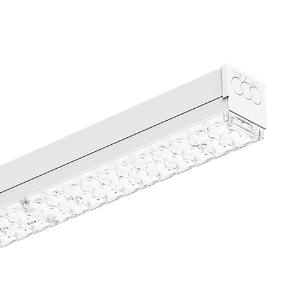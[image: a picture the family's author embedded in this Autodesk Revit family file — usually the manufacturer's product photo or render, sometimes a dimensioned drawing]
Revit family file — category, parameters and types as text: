
# Revit family: 3f_filippi_-_3f_zeta_l_ugr_3f_filippi_-_10841_-_3f_zeta_l_ugr_40-940_led_dali_l1489
name_source: partatom
category: Lighting Fixtures
units: mm (PartAtom-declared; Revit-internal decimal feet)

## family parameters
Cut with Voids When Loaded = No
Host = Face
Light Source = No
Part Type = Normal
Room Calculation Point = No
Round Connector Dimension = Use Diameter
Shared = No

## types (1)
- 3F Filippi - 3F Zeta L UGR (1 x LED, 5310 lm, 40 W, 4000 K)
    Apparent Load = 40 VA
    Approval mark = ENEC
    CIE Flux Codes = 83 96 99 97 100
    Color Rendering = 90
    Color Temperature = 4000 K
    Control Gear = Electronic transformer
    Default Elevation = 1800 mm
    Description = ILLUMINOTECHNICAL
Luminous efficiency 100% (DLOR 97%, ULOR 3%).
Initial luminous flux of the luminaire 5310 lm.
Controlled direct symmetric distribution.
Installation Interdistance Transv.D = 1.39 x hu - Long.D = 1.30 x hu.
Average luminance <3000 cd/m² for radial angles >65°.
Tabular UGR (CIE 117 - 4H-8H; S=0.25H; 70/50/20): RUG 18.3 - 16.7.
Beam angle: 78° - 75°.
Luminous efficacy 133 lm/W.
Lifetime (L93/B10): 30000 h. (tq+25°C)
Lifetime (L90/B10): 50000 h. (tq+25°C)
Lifetime (L85/B10): 80000 h. (tq+25°C)
Lifetime (L80/B10): 100000 h. (tq+25°C)
Sudden decreased luminous flux after 50000 hours: 0% (C0).
Photobiological safety in compliance with IEC/TR 62778: RG0 risk exempt, (IEC 62471).
In compliance with IEC/EN 62722-2-1 - IEC/EN 62717 standards.

SOURCE
Linear LED module 40W/940.
Energy efficiency class (UE 2019/2020 - UE 2019/2015): E.
CIE 13.3 Colour rendering index: CRI >90 (R9 >50%).
IES TM-30 Fidelity Index: Rf = 92 Rg = 101.
CCT nominal colour temperature 4000 K.
Colour initial tolerance (MacAdam): SDCM 3.

MECHANICAL
Housing in hot-galvanised steel, painted in white polyester, obtained through rolling process.
Light unit in hot-galvanised steel, painted in white polyester base with fixing springs and retractable safety hooks in stainless steel.
Transparent methacrylate (PMMA) controlled distribution lenses with flat external surface.
End caps in white polycarbonate.
Pair of stainless steel sliding brackets with sliding block screws.
Luminaire with limited surface temperature. - D - (EN 60598-2-24)
Dimensions: 1489x62 mm, height 65 mm. Weight 3.555 kg.
IP40 protection degree.
Mechanical strength to impacts IK06 (1 joule).
Glow-wire test resistance 650°C.

ELECTRICAL
Halogen Free DALI-2, PUSH-DIM, electronic wiring 230V-50/60Hz, power factor 0.95 at full load, THD <25%, constant output current, class I, 1 driver, 1 DALI addresse.
Power of the luminaire 40 W.
CE - IEC 60598-1 - EN 60598-1.
SAFE FLICKER: PstLM=<1 and SVM=<0.4 (IEC TR 61547-1 and IEC TR 63158), to ensure a more comfortable and safe light.
Luminaire compliant with EN 60598-2-22 for power supply from a centralised emergency system CPSS (Central Power Supply System), not incorporated in the luminaire - high risk areas excluded. The default power and flux are 100% in AC and 15% in DC.
Ambient temperature from 0°C to +25°C.
Temperature class T6 max 85°C.
Relative humidity UR: <85%.

INSTALLATION
Ceiling / Suspended / Wall.
All accessories dedicated to this product are available on the Catalog and on our website www.3F-Filippi.com.

APPLICATIONS
Suitable product for food production plants (HACCP), IFS (Food Version 6), BRC (GSFS Food Version 7).
In commercial environments, exhibition areas, shops and stores.
In environments with VDTs, managerial offices and staterooms, public offices and schools.

LIGHT MANAGEMENT
Recommended minimum setting: 10%.
The device, equipped with DALI-2 driver, can be controlled manually with 3F Easy Dim technology or automatically/manually with 3F Smart Dimming technology and/or centralised DALI systems.
DALI-2 certification guarantees interoperability with other devices with the same certification.
In electrical systems without a regulation system (manual or automatic) and DALI bus, a suitable jumper must be made on the DA-DA terminals of the appliance.

WARNING
Luminaire designed for disposal/recycling at end-of-life.
Replaceable (LED only) light source by a professional. Replaceable control gear by a professional.
    Height = 65 mm
    Lamp = 1 x LED
    Lamp Light Flux = 5310 lm
    Lamp Power = 40 W
    Lamp count = 1
    Length = 1489 mm
    Lifetime = 50000 h
    Luminous efficacy = 133 lm/W
    Manufacturer = 3F Filippi
    ModVariant = No
    Model = 3F Filippi - 10841 - 3F Zeta L UGR 40-940 LED DALI L1489
    Mounting Place = Ceiling
    Mounting Type = Surface mounted
    Number of Poles = 1
    OnlyDefault = Yes
    Power Factor = 1
    Product Name = 3F Filippi - 3F Zeta L UGR
    Product group = ceiling mounted luminaire
    ProductGroupID = 3
    Protection Class = Protection class I
    Protection Degree = IP 40
    RLX_Detail_Level = 1
    RLX_Emergency_Light_Flux = 0 lm
    RLX_Emergency_Type = 0
    RLX_Emergency_Type_DB = No
    RlxData = <blob elided: 50257 chars, md5=2a35839c>
    Socket = socket
    Standby Power = 0 W
    System Light Flux = 5310 lm
    System Power = 40 W
    Type Comments = Product without accessories
    Type Image = 3ffilippi_3f_zeta_l_ugr.jpg
    URL = http://relux.com
    VarID = ---
    Voltage = 0 V
    Weight = 0.00 kg
    Width = 62 mm  [stored 0.203412 ft]

note: [stored X ft] marks values corroborated as IEEE doubles in the binary element streams (Revit-internal decimal feet)

## geometry (parser evidence)
native form markers: Blend x4, Sweep x11
no freeform markers — native parametric forms only
